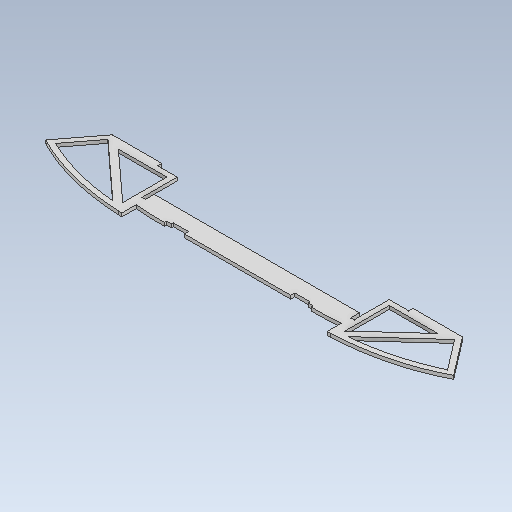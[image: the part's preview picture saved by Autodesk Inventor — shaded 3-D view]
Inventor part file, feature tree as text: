
AUTODESK INVENTOR PART (.ipt)
format: ipt  version: 2020.3 (Build 243373010, 373A)  size: 198,144 bytes
history: native  units: in
note: dims shown in document units (in); Inventor stores cm internally (conversion verified against a paired STEP export)
features: other x3, extrude x1, mirror x1, sketch x1
ambient origin geometry x8: Origin, YZ Plane, XZ Plane, XY Plane, X Axis, Y Axis, Z Axis, Center Point
bodies: Solid1 (feature_tree)
feature tree (6):
  other  "bulkhead_front"
  other  "base_sketch.ipt"
  extrude  "Extrusion1"  Depth=0.1575in
  mirror  "Mirror1"
  other  "bulkhead_front_plane"
  sketch  "Sketch2"  dims[d0=0.3937in d1=0.1181in d2=0.1181in d3=0.1181in d4=0.1575in d5=0.1181in d6=0.0787in d7=0.0787in d8=0.0in d11=0.0472in d12=0.0472in d13=0.2362in d14=0.2362in]
